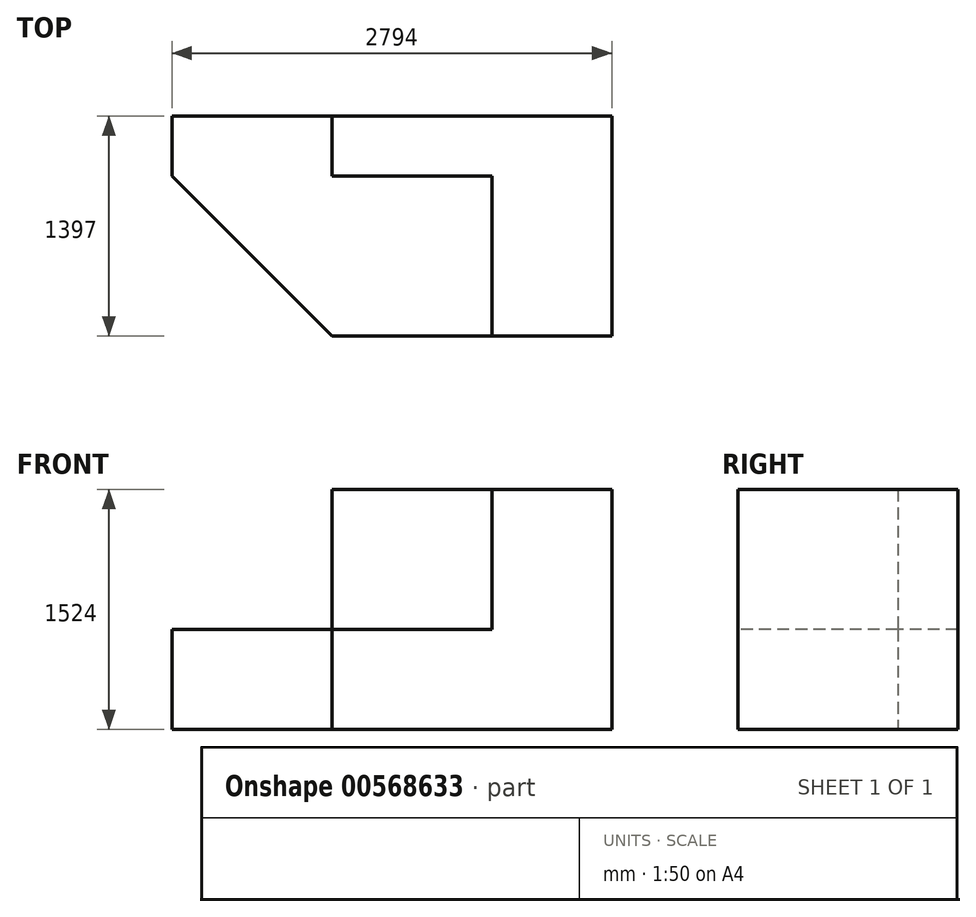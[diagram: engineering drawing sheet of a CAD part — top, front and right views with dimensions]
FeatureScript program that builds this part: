
annotation { "Feature Type Name" : "Feature", "Feature Type Description" : "" }
export const myFeature = defineFeature(function(context is Context, id is Id, definition is map)
    precondition{}
    {
        {
            var Q0;
            Q0=qCreatedBy(makeId("Top.planeOp"),FACE);
            var sketch = newSketch(context, id + "F0", { "sketchPlane" : qUnion([Q0])});
            skLineSegment(sketch, "E0", {"start": v(0, 0) * mm, "end": v(0, 1397) * mm});
            skLineSegment(sketch, "E1", {"start": v(0, 1397) * mm, "end": v(-1778, 1397) * mm});
            skLineSegment(sketch, "E2", {"start": v(-1778, 1397) * mm, "end": v(-1778, 1016) * mm});
            skLineSegment(sketch, "E3", {"start": v(-1778, 1016) * mm, "end": v(-762, 1016) * mm});
            skLineSegment(sketch, "E4", {"start": v(-762, 1016) * mm, "end": v(-762, 0) * mm});
            skLineSegment(sketch, "E5", {"start": v(-762, 0) * mm, "end": v(0, 0) * mm});
            skLineSegment(sketch, "E6", {"start": v(-762, 0) * mm, "end": v(-1778, 0) * mm});
            skLineSegment(sketch, "E7", {"start": v(-1778, 0) * mm, "end": v(-762, 0) * mm});
            skLineSegment(sketch, "E8", {"start": v(-762, 1016) * mm, "end": v(-1778, 1016) * mm});
            skLineSegment(sketch, "E9", {"start": v(-1778, 1397) * mm, "end": v(-2794, 1397) * mm});
            skLineSegment(sketch, "E10", {"start": v(-2794, 1397) * mm, "end": v(-2794, 1016) * mm});
            skLineSegment(sketch, "E11", {"start": v(-2794, 1016) * mm, "end": v(-1778, 0) * mm});
            skSolve(sketch);
        }
        {
            var Q0;
            Q0=makeQuery(id+"F0.imprint","IMPRINT",FACE,{"disambiguationData":[TD([[makeQuery(id+"F0.imprint","IMPRINT",EDGE,{"derivedFrom":sQuery(id+"F0.wireOp",EDGE,"E0")}),1.0]])]});
            extrude(context, id + "F1", {"entities" : qUnion([Q0]), "depth" : 1524 * mm, "offsetDistance" : 25.4 * mm});
        }
        {
            var Q0;
            Q0=makeQuery(id+"F1.opExtrude","CAP_FACE",FACE,{"disambiguationData":[OSD([sQuery(id+"F0.wireOp",EDGE,"E0"),sQuery(id+"F0.wireOp",EDGE,"E1"),sQuery(id+"F0.wireOp",EDGE,"E2"),sQuery(id+"F0.wireOp",EDGE,"E4"),sQuery(id+"F0.wireOp",EDGE,"E5"),sQuery(id+"F0.wireOp",EDGE,"E8")])],"isStart":true});
            var sketch = newSketch(context, id + "F2", { "sketchPlane" : qUnion([Q0])});
            skLineSegment(sketch, "E12", {"start": v(-1778, -1397) * mm, "end": v(-2794, -1397) * mm});
            skLineSegment(sketch, "E13", {"start": v(-2794, -1397) * mm, "end": v(-2794, -1016) * mm});
            skLineSegment(sketch, "E14", {"start": v(-2794, -1016) * mm, "end": v(-2794, -1397) * mm});
            skLineSegment(sketch, "E15", {"start": v(-1778, -1397) * mm, "end": v(-1778, -1016) * mm});
            skLineSegment(sketch, "E16", {"start": v(-1778, -1016) * mm, "end": v(-762, -1016) * mm});
            skLineSegment(sketch, "E17", {"start": v(-762, -1016) * mm, "end": v(-762, 0) * mm});
            skLineSegment(sketch, "E18", {"start": v(-762, 0) * mm, "end": v(-1778, 0) * mm});
            skLineSegment(sketch, "E19", {"start": v(-1778, 0) * mm, "end": v(-2794, -1016) * mm});
            skSolve(sketch);
        }
        {
            var Q0;
            Q0=makeQuery(id+"F2.imprint","IMPRINT",FACE,{"disambiguationData":[TD([[makeQuery(id+"F2.imprint","IMPRINT",EDGE,{"derivedFrom":sQuery(id+"F2.wireOp",EDGE,"E12")}),-1.0]])]});
            extrude(context, id + "F3", {"entities" : qUnion([Q0]), "operationType" : NewBodyOperationType.ADD, "oppositeDirection" : true, "depth" : 635 * mm, "offsetDistance" : 25.4 * mm});
        }
    });
